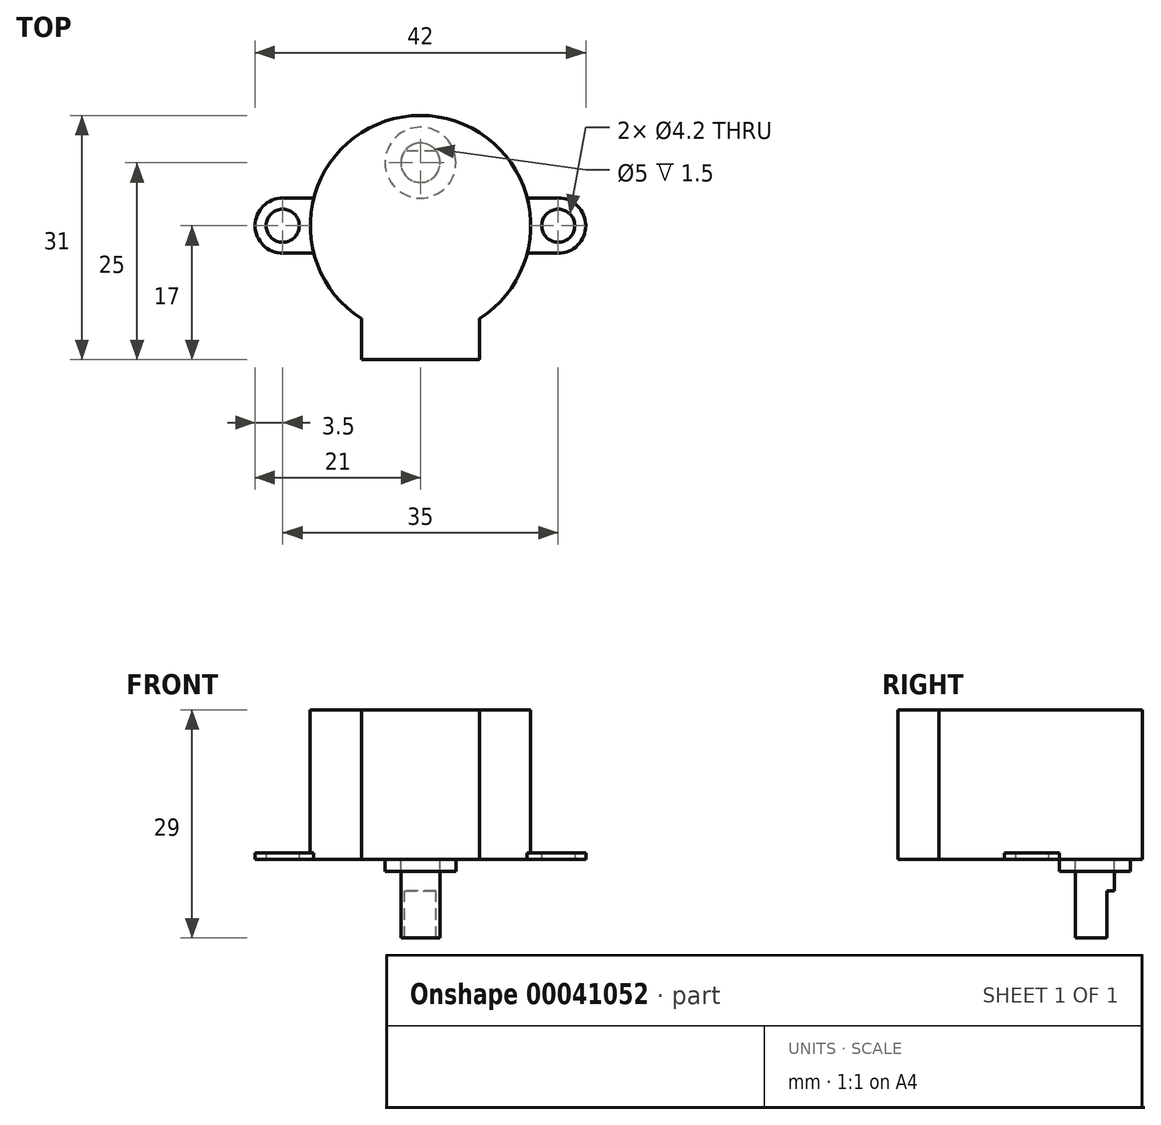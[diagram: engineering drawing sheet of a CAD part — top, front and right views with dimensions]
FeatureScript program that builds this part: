
annotation { "Feature Type Name" : "Feature", "Feature Type Description" : "" }
export const myFeature = defineFeature(function(context is Context, id is Id, definition is map)
    precondition{}
    {
        {
            var Q0;
            Q0=qCreatedBy(makeId("Top.planeOp"),FACE);
            var sketch = newSketch(context, id + "F0", { "sketchPlane" : qUnion([Q0])});
            skArc(sketch, "E0", {"start": v(7.5, -11.82) * mm, "mid": v(0, 14) * mm, "end": v(-7.5, -11.82) * mm});
            skCircle(sketch, "E1", {"center": v(-17.5, 0) * mm, "radius": 2.1 * mm});
            skCircle(sketch, "E2", {"center": v(17.5, 0) * mm, "radius": 2.1 * mm});
            skCircle(sketch, "E3", {"center": v(0, 8) * mm, "radius": 4.5 * mm});
            skArc(sketch, "E4", {"start": v(17.5, -3.5) * mm, "mid": v(21, 0) * mm, "end": v(17.5, 3.5) * mm});
            skArc(sketch, "E5", {"start": v(-17.5, 3.5) * mm, "mid": v(-21, 0) * mm, "end": v(-17.5, -3.5) * mm});
            skLineSegment(sketch, "E6", {"start": v(17.5, -3.5) * mm, "end": v(13.56, -3.5) * mm});
            skLineSegment(sketch, "E7", {"start": v(-17.5, 3.5) * mm, "end": v(-13.56, 3.5) * mm});
            skLineSegment(sketch, "E8.rect.bottom", {"start": v(7.5, -17) * mm, "end": v(-7.5, -17) * mm});
            skLineSegment(sketch, "E8.rect.left", {"start": v(7.5, -17) * mm, "end": v(7.5, -11.82) * mm});
            skLineSegment(sketch, "E8.rect.right", {"start": v(-7.5, -17) * mm, "end": v(-7.5, -11.82) * mm});
            skPoint(sketch, "E9.orphan", {"position": v(-7.5, 17) * mm});
            skPoint(sketch, "E10.orphan", {"position": v(7.5, 17) * mm});
            skLineSegment(sketch, "E11.trimOffspring", {"start": v(13.56, 3.5) * mm, "end": v(17.5, 3.5) * mm});
            skLineSegment(sketch, "E12.trimOffspring", {"start": v(-13.56, -3.5) * mm, "end": v(-17.5, -3.5) * mm});
            skCircle(sketch, "E13", {"center": v(0, 8) * mm, "radius": 2.5 * mm});
            skSolve(sketch);
        }
        {
            var Q0;
            Q0=makeQuery(id+"F0.imprint","IMPRINT",FACE,{"disambiguationData":[TD([[makeQuery(id+"F0.imprint","IMPRINT",EDGE,{"derivedFrom":sQuery(id+"F0.wireOp",EDGE,"E3")}),-1.0]])]});
            var Q1;
            Q1=makeQuery(id+"F0.imprint","IMPRINT",FACE,{"disambiguationData":[TD([[makeQuery(id+"F0.imprint","IMPRINT",EDGE,{"derivedFrom":sQuery(id+"F0.wireOp",EDGE,"E3")}),1.0]])]});
            var Q2;
            Q2=makeQuery(id+"F0.imprint","IMPRINT",FACE,{"disambiguationData":[TD([[makeQuery(id+"F0.imprint","IMPRINT",EDGE,{"derivedFrom":sQuery(id+"F0.wireOp",EDGE,"E13")}),1.0]])]});
            extrude(context, id + "F1", {"entities" : qUnion([Q0, Q1, Q2]), "depth" : 19 * mm});
        }
        {
            var Q0;
            Q0=makeQuery(id+"F0.imprint","IMPRINT",FACE,{"disambiguationData":[TD([[makeQuery(id+"F0.imprint","IMPRINT",EDGE,{"derivedFrom":sQuery(id+"F0.wireOp",EDGE,"E1")}),-1.0]])]});
            var Q1;
            Q1=makeQuery(id+"F0.imprint","IMPRINT",FACE,{"disambiguationData":[TD([[makeQuery(id+"F0.imprint","IMPRINT",EDGE,{"derivedFrom":sQuery(id+"F0.wireOp",EDGE,"E2")}),-1.0]])]});
            extrude(context, id + "F2", {"entities" : qUnion([Q0, Q1]), "operationType" : NewBodyOperationType.ADD, "depth" : 0.8 * mm});
        }
        {
            var Q0;
            Q0=makeQuery(id+"F0.imprint","IMPRINT",FACE,{"disambiguationData":[TD([[makeQuery(id+"F0.imprint","IMPRINT",EDGE,{"derivedFrom":sQuery(id+"F0.wireOp",EDGE,"E3")}),1.0]])]});
            extrude(context, id + "F3", {"entities" : qUnion([Q0]), "operationType" : NewBodyOperationType.ADD, "oppositeDirection" : true, "depth" : 1.5 * mm});
        }
        {
            var Q0;
            Q0=makeQuery(id+"F0.imprint","IMPRINT",FACE,{"disambiguationData":[TD([[makeQuery(id+"F0.imprint","IMPRINT",EDGE,{"derivedFrom":sQuery(id+"F0.wireOp",EDGE,"E13")}),1.0]])]});
            extrude(context, id + "F4", {"entities" : qUnion([Q0]), "oppositeDirection" : true, "depth" : 10 * mm});
        }
        {
            var Q0;
            Q0=makeQuery(id+"F4.opExtrude","CAP_FACE",FACE,{"disambiguationData":[OSD([sQuery(id+"F0.wireOp",EDGE,"E13")])],"isStart":false});
            var sketch = newSketch(context, id + "F5", { "sketchPlane" : qUnion([Q0])});
            skLineSegment(sketch, "E14.rect.bottom", {"start": v(2.91, -9.5) * mm, "end": v(-2.91, -9.5) * mm});
            skLineSegment(sketch, "E14.rect.top", {"start": v(2.91, -6.5) * mm, "end": v(-2.91, -6.5) * mm});
            skLineSegment(sketch, "E14.rect.left", {"start": v(2.91, -9.5) * mm, "end": v(2.91, -6.5) * mm});
            skLineSegment(sketch, "E14.rect.right", {"start": v(-2.91, -9.5) * mm, "end": v(-2.91, -6.5) * mm});
            skPoint(sketch, "E14.rect.middle", {"position": v(0, -8) * mm});
            skLineSegment(sketch, "E15.bottom", {"start": v(-2.91, -6.5) * mm, "end": v(2.91, -6.5) * mm});
            skLineSegment(sketch, "E15.top", {"start": v(-2.91, -5.02) * mm, "end": v(2.91, -5.02) * mm});
            skLineSegment(sketch, "E15.left", {"start": v(-2.91, -6.5) * mm, "end": v(-2.91, -5.02) * mm});
            skLineSegment(sketch, "E15.right", {"start": v(2.91, -6.5) * mm, "end": v(2.91, -5.02) * mm});
            skLineSegment(sketch, "E16.top", {"start": v(2.91, -10.83) * mm, "end": v(-2.91, -10.83) * mm});
            skLineSegment(sketch, "E16.left", {"start": v(2.91, -9.5) * mm, "end": v(2.91, -10.83) * mm});
            skLineSegment(sketch, "E16.right", {"start": v(-2.91, -9.5) * mm, "end": v(-2.91, -10.83) * mm});
            skSolve(sketch);
        }
        {
            var Q0;
            Q0=makeQuery(id+"F5.imprint","IMPRINT",FACE,{"disambiguationData":[TD([[makeQuery(id+"F5.imprint","IMPRINT",EDGE,{"derivedFrom":sQuery(id+"F5.wireOp",EDGE,"E15.top")}),-1.0]])]});
            var Q1;
            {var subQ0=makeQuery(id+"F4.opExtrude","CAP_EDGE",EDGE,{"disambiguationData":[OSD([sQuery(id+"F0.wireOp",EDGE,"E13")])],"isStart":false});var subQ1=sQuery(id+"F5.wireOp",EDGE,"E15.bottom");var subQ3=makeQuery(id+"F5.imprint","INTERSECT",VERTEX,{"disambiguationData":[OD(0.0)],"derivedFrom":[subQ0,subQ1]});Q1=makeQuery(id+"F5.imprint","IMPRINT",FACE,{"disambiguationData":[TD([[makeQuery(id+"F5.imprint","IMPRINT",EDGE,{"disambiguationData":[TD([[subQ3,-1.0]])],"derivedFrom":subQ1}),1.0]])]});}
            var Q2;
            {var subQ0=makeQuery(id+"F4.opExtrude","CAP_EDGE",EDGE,{"disambiguationData":[OSD([sQuery(id+"F0.wireOp",EDGE,"E13")])],"isStart":false});var subQ1=sQuery(id+"F5.wireOp",EDGE,"E14.rect.bottom");var subQ3=makeQuery(id+"F5.imprint","INTERSECT",VERTEX,{"disambiguationData":[OD(0.0)],"derivedFrom":[subQ0,subQ1]});Q2=makeQuery(id+"F5.imprint","IMPRINT",FACE,{"disambiguationData":[TD([[makeQuery(id+"F5.imprint","IMPRINT",EDGE,{"disambiguationData":[TD([[subQ3,-1.0]])],"derivedFrom":subQ1}),1.0]])]});}
            var Q3;
            Q3=makeQuery(id+"F5.imprint","IMPRINT",FACE,{"disambiguationData":[TD([[makeQuery(id+"F5.imprint","IMPRINT",EDGE,{"derivedFrom":sQuery(id+"F5.wireOp",EDGE,"E16.top")}),-1.0]])]});
            extrude(context, id + "F6", {"entities" : qUnion([Q0, Q1, Q2, Q3]), "oppositeDirection" : true, "depth" : 6 * mm});
        }
        {
            var Q0;
            Q0=makeQuery(id+"F6.opExtrude","SWEPT_BODY",BODY,{"disambiguationData":[OSD([sQuery(id+"F5.wireOp",EDGE,"E15.bottom"),sQuery(id+"F5.wireOp",EDGE,"E15.top"),sQuery(id+"F5.wireOp",EDGE,"E15.left"),sQuery(id+"F5.wireOp",EDGE,"E15.right")])]});
            var Q1;
            Q1=makeQuery(id+"F6.opExtrude","SWEPT_BODY",BODY,{"disambiguationData":[OSD([sQuery(id+"F5.wireOp",EDGE,"E14.rect.bottom"),sQuery(id+"F5.wireOp",EDGE,"E16.top"),sQuery(id+"F5.wireOp",EDGE,"E16.left"),sQuery(id+"F5.wireOp",EDGE,"E16.right")])]});
            var Q2;
            Q2=makeQuery(id+"F4.opExtrude","SWEPT_BODY",BODY,{"disambiguationData":[OSD([sQuery(id+"F0.wireOp",EDGE,"E13")])]});
            booleanBodies(context, id + "F7", {"operationType" : BooleanOperationType.SUBTRACTION, "tools" : qUnion([Q0, Q1]), "targets" : qUnion([Q2])});
        }
    });
